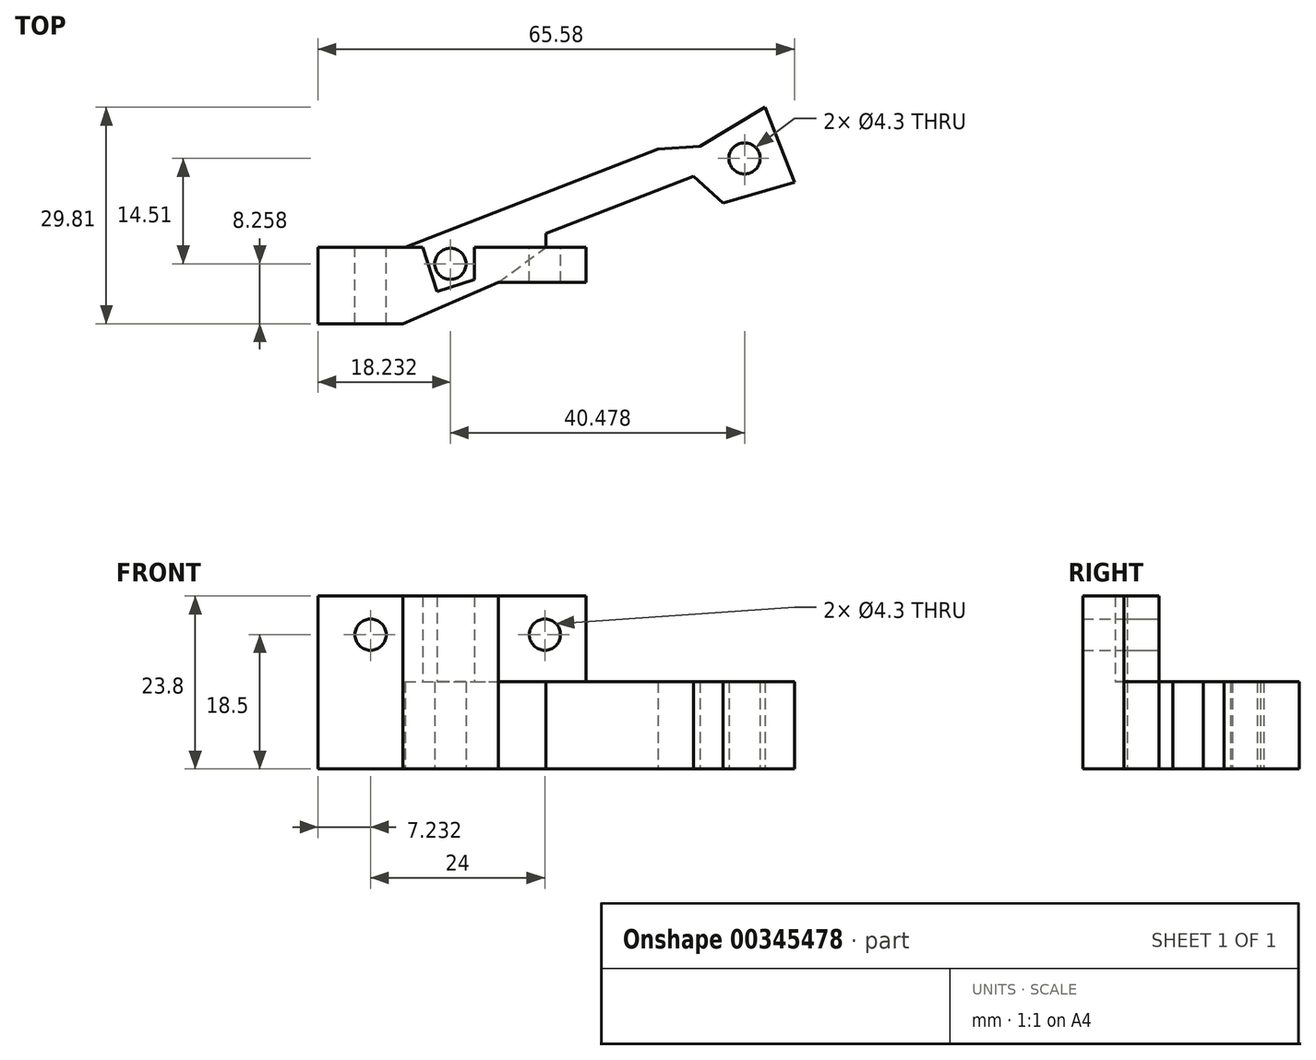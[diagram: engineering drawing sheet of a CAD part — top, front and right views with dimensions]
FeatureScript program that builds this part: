
annotation { "Feature Type Name" : "Feature", "Feature Type Description" : "" }
export const myFeature = defineFeature(function(context is Context, id is Id, definition is map)
    precondition{}
    {
        {
            var Q0;
            Q0=qCreatedBy(makeId("Top.planeOp"),FACE);
            var sketch = newSketch(context, id + "F0", { "sketchPlane" : qUnion([Q0])});
            skCircle(sketch, "E0", {"center": v(-21.75, -8.36) * mm, "radius": 2.15 * mm});
            skLineSegment(sketch, "E1.left", {"start": v(-39.98, -16.62) * mm, "end": v(-39.98, -6.1) * mm});
            skLineSegment(sketch, "E2", {"start": v(-39.98, -16.62) * mm, "end": v(-28.31, -16.62) * mm});
            skLineSegment(sketch, "E3", {"start": v(11.8, 11.1) * mm, "end": v(17.66, 3.28) * mm, "construction": true});
            skLineSegment(sketch, "E4", {"start": v(0, -6.1) * mm, "end": v(19.88, -6.1) * mm, "construction": true});
            skCircle(sketch, "E5", {"center": v(-21.75, -8.36) * mm, "radius": 40 * mm, "construction": true});
            skLineSegment(sketch, "E6", {"start": v(-3.61, 5.1) * mm, "end": v(30.01, 5.1) * mm, "construction": true});
            skCircle(sketch, "E7", {"center": v(15.9, 5.13) * mm, "radius": 2.15 * mm, "construction": true});
            skLineSegment(sketch, "E8", {"start": v(17.66, 3.28) * mm, "end": v(-21.31, -25.95) * mm, "construction": true});
            skLineSegment(sketch, "E9", {"start": v(-28.31, -16.62) * mm, "end": v(-21.31, -25.95) * mm, "construction": true});
            skLineSegment(sketch, "E10", {"start": v(-3.12, -10.92) * mm, "end": v(-3.12, -6.1) * mm});
            skLineSegment(sketch, "E11", {"start": v(-39.98, -6.1) * mm, "end": v(-3.12, -6.1) * mm});
            skLineSegment(sketch, "E12", {"start": v(-3.12, -10.92) * mm, "end": v(-15.18, -10.92) * mm});
            skLineSegment(sketch, "E13", {"start": v(-15.18, -10.92) * mm, "end": v(-28.31, -16.62) * mm});
            skPoint(sketch, "E14", {"position": v(-21.75, -13.77) * mm});
            skCircle(sketch, "E15", {"center": v(18.73, 6.15) * mm, "radius": 2.15 * mm});
            skLineSegment(sketch, "E16", {"start": v(-28, -6.1) * mm, "end": v(21.58, 13.19) * mm});
            skLineSegment(sketch, "E17", {"start": v(21.58, 13.19) * mm, "end": v(25.6, 2.86) * mm});
            skLineSegment(sketch, "E18", {"start": v(-25.58, -6.1) * mm, "end": v(-23.62, -12.18) * mm});
            skLineSegment(sketch, "E19", {"start": v(-23.62, -12.18) * mm, "end": v(-18.45, -10.5) * mm});
            skLineSegment(sketch, "E20", {"start": v(-18.45, -10.5) * mm, "end": v(-18.45, -6.1) * mm});
            skLineSegment(sketch, "E21", {"start": v(-28, -6.1) * mm, "end": v(-28.31, -16.62) * mm});
            skLineSegment(sketch, "E22", {"start": v(-15.18, -10.92) * mm, "end": v(-8.61, -6.1) * mm});
            skLineSegment(sketch, "E23", {"start": v(-8.61, -6.1) * mm, "end": v(-8.61, -4.2) * mm});
            skLineSegment(sketch, "E24", {"start": v(-8.61, -4.2) * mm, "end": v(11.7, 3.71) * mm});
            skLineSegment(sketch, "E25", {"start": v(11.7, 3.71) * mm, "end": v(15.77, 0) * mm});
            skLineSegment(sketch, "E26", {"start": v(15.77, 0) * mm, "end": v(25.6, 2.86) * mm});
            skLineSegment(sketch, "E27", {"start": v(6.8, 7.43) * mm, "end": v(12.57, 7.84) * mm});
            skLineSegment(sketch, "E28", {"start": v(12.57, 7.84) * mm, "end": v(21.58, 13.19) * mm});
            skSolve(sketch);
        }
        {
            var Q0;
            Q0=qCreatedBy(makeId("Front.planeOp"),FACE);
            var sketch = newSketch(context, id + "F1", { "sketchPlane" : qUnion([Q0])});
            skCircle(sketch, "E29", {"center": v(-32.75, 18.5) * mm, "radius": 2.15 * mm});
            skCircle(sketch, "E30", {"center": v(-8.75, 18.5) * mm, "radius": 2.15 * mm});
            skSolve(sketch);
        }
        {
            var Q0;
            {var subQ5=sQuery(id+"F0.wireOp",EDGE,"E18");Q0=makeQuery(id+"F0.imprint","IMPRINT",FACE,{"disambiguationData":[TD([[makeQuery(id+"F0.imprint","IMPRINT",EDGE,{"derivedFrom":subQ5}),-1.0]])]});}
            var Q1;
            {var subQ0=sQuery(id+"F0.wireOp",EDGE,"E12");var subQ1=sQuery(id+"F0.wireOp",EDGE,"E10");var subQ2=makeQuery(id+"F0.imprint","INTERSECT",VERTEX,{"derivedFrom":[subQ1,subQ0]});Q1=makeQuery(id+"F0.imprint","IMPRINT",FACE,{"disambiguationData":[TD([[makeQuery(id+"F0.imprint","IMPRINT",EDGE,{"disambiguationData":[TD([[subQ2,-1.0]])],"derivedFrom":subQ1}),1.0]])]});}
            var Q2;
            {var subQ1=sQuery(id+"F0.wireOp",EDGE,"E1.left");Q2=makeQuery(id+"F0.imprint","IMPRINT",FACE,{"disambiguationData":[TD([[makeQuery(id+"F0.imprint","IMPRINT",EDGE,{"derivedFrom":subQ1}),-1.0]])]});}
            extrude(context, id + "F2", {"entities" : qUnion([Q0, Q1, Q2]), "depth" : 23.8 * mm});
        }
        {
            var Q0;
            Q0=makeQuery(id+"F2.opExtrude","SWEPT_FACE",FACE,{"disambiguationData":[OSD([sQuery(id+"F0.wireOp",EDGE,"E2")])]});
            var Q1;
            Q1=makeQuery(id+"F1.imprint","IMPRINT",FACE,{"disambiguationData":[TD([[makeQuery(id+"F1.imprint","IMPRINT",EDGE,{"derivedFrom":sQuery(id+"F1.wireOp",EDGE,"E29")}),1.0]])]});
            var Q2;
            Q2=makeQuery(id+"F1.imprint","IMPRINT",FACE,{"disambiguationData":[TD([[makeQuery(id+"F1.imprint","IMPRINT",EDGE,{"derivedFrom":sQuery(id+"F1.wireOp",EDGE,"E30")}),1.0]])]});
            extrude(context, id + "F3", {"entities" : qUnion([Q0, Q1, Q2]), "operationType" : NewBodyOperationType.REMOVE, "oppositeDirection" : true, "depth" : -25 * mm});
        }
        {
            var Q0;
            Q0=makeQuery(id+"F0.imprint","IMPRINT",FACE,{"disambiguationData":[TD([[makeQuery(id+"F0.imprint","IMPRINT",EDGE,{"derivedFrom":sQuery(id+"F0.wireOp",EDGE,"E15")}),-1.0]])]});
            var Q1;
            Q1=makeQuery(id+"F0.imprint","IMPRINT",FACE,{"disambiguationData":[TD([[makeQuery(id+"F0.imprint","IMPRINT",EDGE,{"derivedFrom":sQuery(id+"F0.wireOp",EDGE,"E0")}),-1.0]])]});
            extrude(context, id + "F4", {"entities" : qUnion([Q0, Q1]), "operationType" : NewBodyOperationType.ADD, "depth" : 12 * mm});
        }
        {
            var Q0;
            {var subQ0=sQuery(id+"F0.wireOp",EDGE,"E10");Q0=makeQuery(id+"F0.imprint","IMPRINT",FACE,{"disambiguationData":[TD([[makeQuery(id+"F0.imprint","IMPRINT",EDGE,{"derivedFrom":subQ0}),1.0]])]});}
            extrude(context, id + "F5", {"entities" : qUnion([Q0]), "operationType" : NewBodyOperationType.REMOVE, "oppositeDirection" : true, "depth" : -12 * mm});
        }
    });
